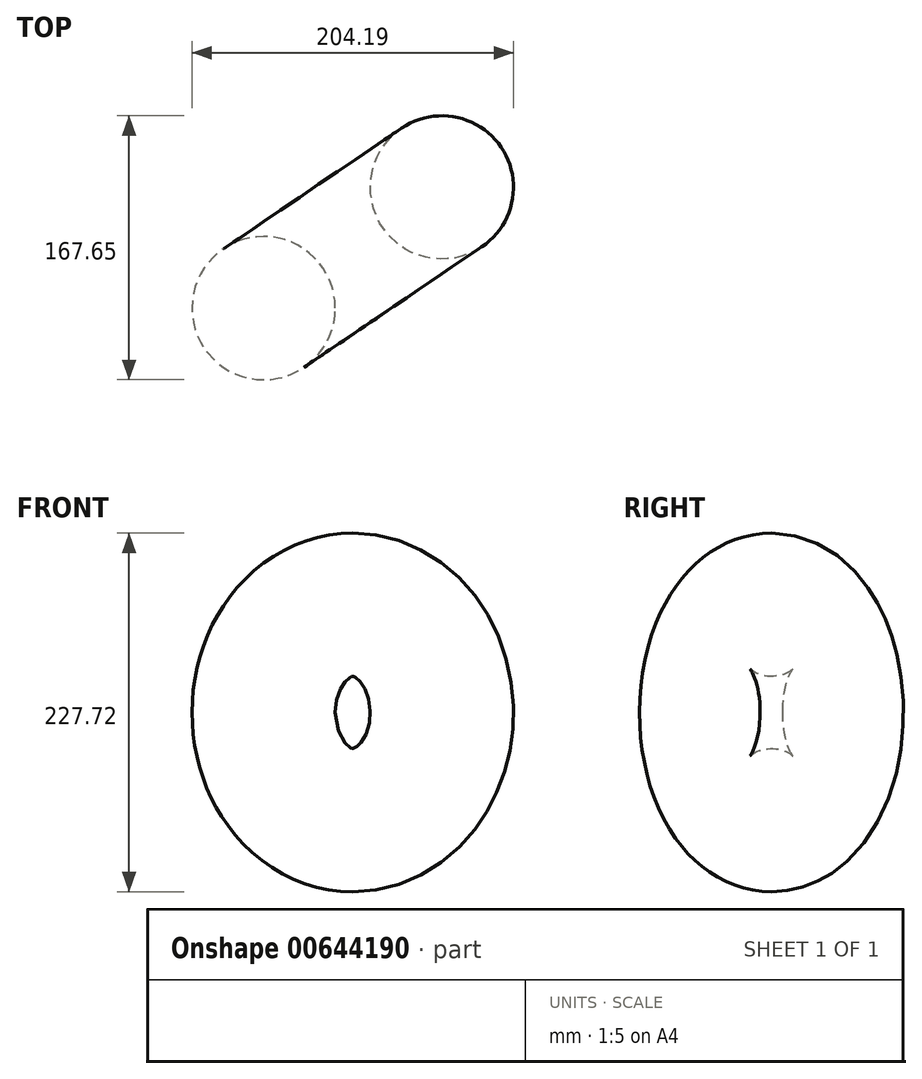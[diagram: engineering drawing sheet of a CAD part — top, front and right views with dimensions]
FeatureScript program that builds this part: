
annotation { "Feature Type Name" : "Feature", "Feature Type Description" : "" }
export const myFeature = defineFeature(function(context is Context, id is Id, definition is map)
    precondition{}
    {
        {
            var Q0;
            Q0=qCreatedBy(makeId("Top.planeOp"),FACE);
            var sketch = newSketch(context, id + "F0", { "sketchPlane" : qUnion([Q0])});
            skCircle(sketch, "E0", {"center": v(-64.33, -37.14) * mm, "radius": 45.5 * mm});
            skLineSegment(sketch, "E1", {"start": v(-44.85, 56.01) * mm, "end": v(35.35, -62.4) * mm});
            skSolve(sketch);
        }
        {
            var Q0;
            Q0=makeQuery(id+"F0.imprint","IMPRINT",FACE,{"disambiguationData":[TD([[makeQuery(id+"F0.imprint","IMPRINT",EDGE,{"derivedFrom":sQuery(id+"F0.wireOp",EDGE,"E0")}),1.0]])]});
            var Q1;
            Q1=sQuery(id+"F0.wireOp",EDGE,"E1");
            revolve(context, id + "F1", {"entities" : qUnion([Q0]), "axis" : qUnion([Q1]), "revolveType" : RevolveType.FULL});
        }
    });
